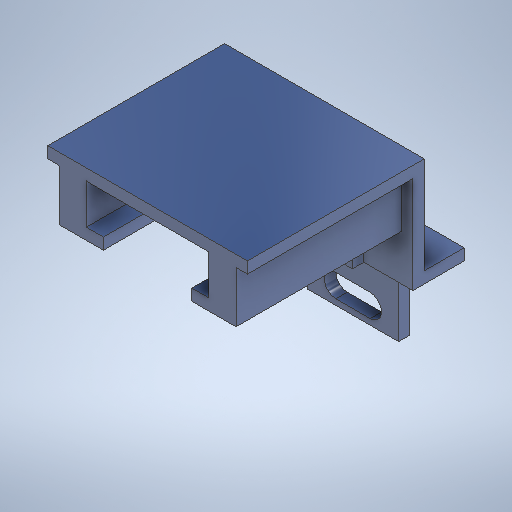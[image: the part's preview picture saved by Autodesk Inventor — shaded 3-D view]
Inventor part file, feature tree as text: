
AUTODESK INVENTOR PART (.ipt)
format: ipt  version: 2025.1 (Build 291241020, 241B)  size: 422,912 bytes
history: native  units: in
note: dims shown in document units (in); Inventor stores cm internally (conversion verified against a paired STEP export)
features: sketch x10, extrude x9, projected_geometry x3
ambient origin geometry x8: Origin, YZ Plane, XZ Plane, XY Plane, X Axis, Y Axis, Z Axis, Center Point
bodies: Solid1 (feature_tree)
feature tree (22):
  extrude  "Extrusion1"  Depth=1.378in
  extrude  "Extrusion2"  Depth=0.0787in
  extrude  "Extrusion3"  Depth=0.1181in
  extrude  "Extrusion4"  Depth=1.1417in TaperAngle=0.0deg
  extrude  "Extrusion5"  Depth=0.6693in TaperAngle=0.0deg
  extrude  "Extrusion6"  Depth=0.6693in TaperAngle=0.0deg
  extrude  "Extrusion7"  Depth=0.0787in TaperAngle=0.0deg
  extrude  "Extrusion8"  Depth=0.4724in TaperAngle=0.0deg
  extrude  "Extrusion10"  Depth=0.0787in
  sketch  "Sketch11"  dims[d28=0.2756in d29=0.0787in d30=0.0in d31=0.0in d32=0.6299in d33=0.0787in d34=0.6299in d35=0.0in d36=0.3937in d37=0.1575in d38=0.0394in d39=0.6299in d40=0.0in d44=0.0787in d45=0.0787in d46=0.0394in d47=0.0in d48=1.378in d49=0.4331in d50=0.8465in d51=0.2756in d52=0.6102in d53=0.2756in]
  sketch  "Sketch1"  dims[d0=0.8465in d1=1.378in]
  sketch  "Sketch2"  dims[d2=0.0787in d3=0.0787in]
  sketch  "Sketch3"  dims[d4=0.2756in d5=0.1181in]
  sketch  "Sketch4"  dims[d6=0.0787in d7=1.1417in d8=0.0in]
  projected_geometry  "Projected Loop1"
  sketch  "Sketch5"  dims[d9=0.0787in d10=0.6693in d11=0.0in]
  sketch  "Sketch6"  dims[d13=0.3543in d14=0.6693in d15=0.0in]
  sketch  "Sketch7"  dims[d16=0.0787in d17=0.0787in d18=0.2559in d19=0.0in d20=0.0in]
  projected_geometry  "Projected Loop2"
  sketch  "Sketch8"  dims[d21=0.0787in d22=0.4724in d23=0.0787in d24=0.0in d25=0.0in]
  sketch  "Sketch10"  dims[d26=0.4173in d27=0.0787in]
  projected_geometry  "Projected Loop4"
